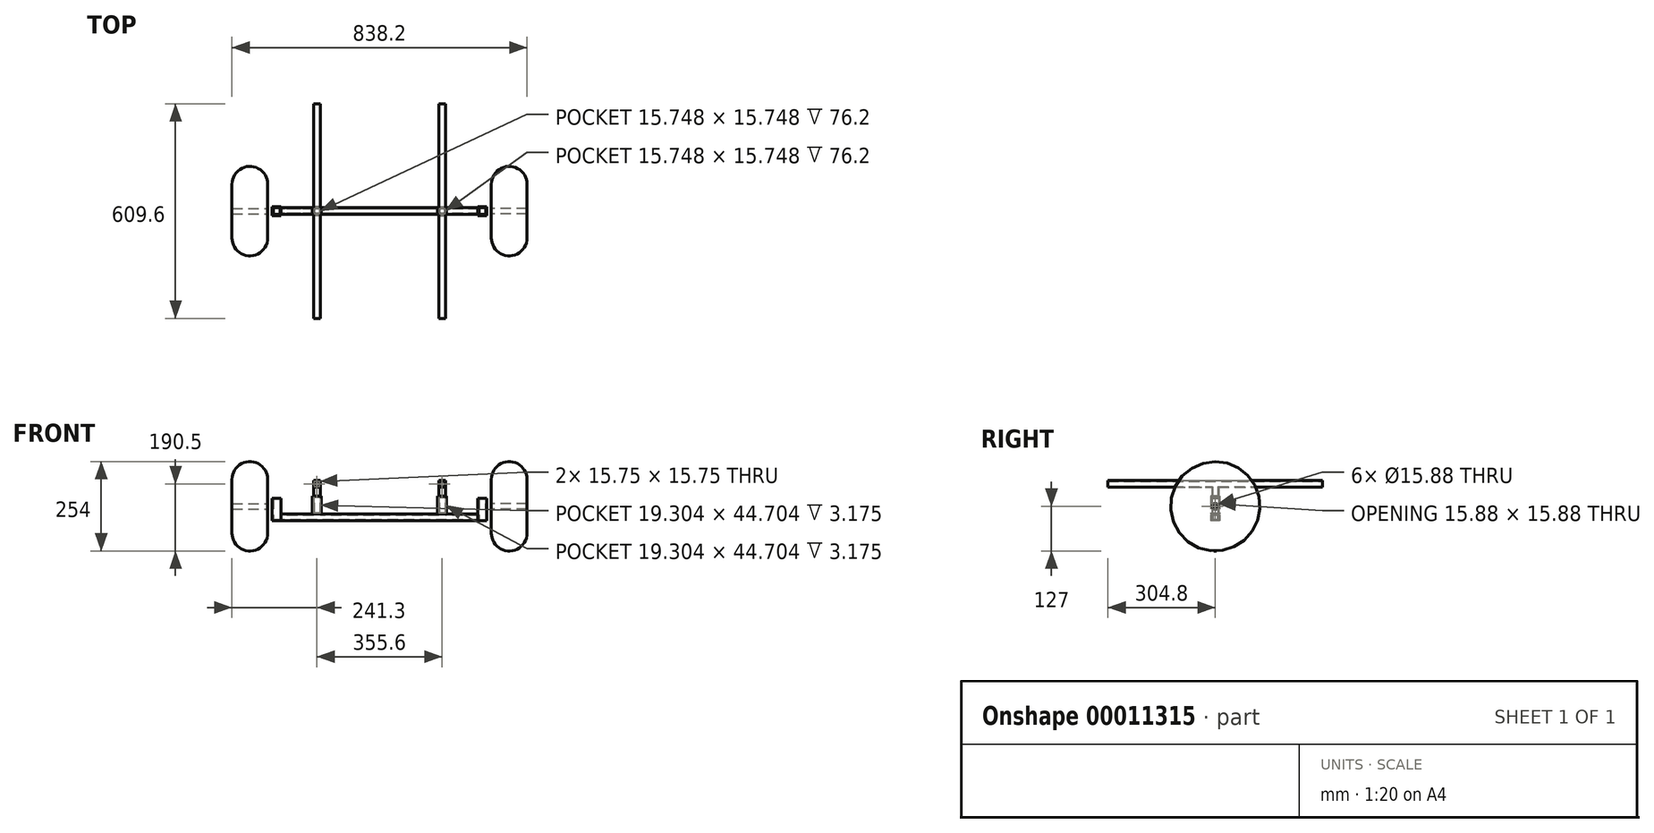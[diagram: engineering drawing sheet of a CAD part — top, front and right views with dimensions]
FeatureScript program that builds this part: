
annotation { "Feature Type Name" : "Feature", "Feature Type Description" : "" }
export const myFeature = defineFeature(function(context is Context, id is Id, definition is map)
    precondition{}
    {
        {
            var Q0;
            Q0=qCreatedBy(makeId("Front.planeOp"),FACE);
            var sketch = newSketch(context, id + "F0", { "sketchPlane" : qUnion([Q0])});
            skLineSegment(sketch, "E0.rect.bottom", {"start": v(279.4, 9.53) * mm, "end": v(-279.4, 9.53) * mm});
            skLineSegment(sketch, "E0.rect.top", {"start": v(279.4, -9.52) * mm, "end": v(-279.4, -9.52) * mm});
            skLineSegment(sketch, "E0.rect.left", {"start": v(279.4, 9.53) * mm, "end": v(279.4, -9.52) * mm});
            skLineSegment(sketch, "E0.rect.right", {"start": v(-279.4, 9.53) * mm, "end": v(-279.4, -9.52) * mm});
            skPoint(sketch, "E0.rect.middle", {"position": v(0, 0) * mm});
            skSolve(sketch);
        }
        {
            var Q0;
            Q0=makeQuery(id+"F0.imprint","IMPRINT",FACE,{"disambiguationData":[TD([[makeQuery(id+"F0.imprint","IMPRINT",EDGE,{"derivedFrom":sQuery(id+"F0.wireOp",EDGE,"E0.rect.bottom")}),1.0]])]});
            extrude(context, id + "F1", {"entities" : qUnion([Q0]), "endBound" : BoundingType.SYMMETRIC, "depth" : 19.05 * mm});
        }
        {
            var Q0;
            Q0=makeQuery(id+"F1.opExtrude","SWEPT_FACE",FACE,{"disambiguationData":[OSD([sQuery(id+"F0.wireOp",EDGE,"E0.rect.top")])]});
            var sketch = newSketch(context, id + "F2", { "sketchPlane" : qUnion([Q0])});
            skLineSegment(sketch, "E1.rect.bottom", {"start": v(-279.4, -12.7) * mm, "end": v(-304.8, -12.7) * mm});
            skLineSegment(sketch, "E1.rect.top", {"start": v(-279.4, 12.7) * mm, "end": v(-304.8, 12.7) * mm});
            skLineSegment(sketch, "E1.rect.left", {"start": v(-279.4, -12.7) * mm, "end": v(-279.4, 12.7) * mm});
            skLineSegment(sketch, "E1.rect.right", {"start": v(-304.8, -12.7) * mm, "end": v(-304.8, 12.7) * mm});
            skPoint(sketch, "E1.rect.middle", {"position": v(-292.1, 0) * mm});
            skLineSegment(sketch, "E2.0", {"start": v(-279.4, 9.53) * mm, "end": v(-279.4, -9.52) * mm, "construction": true});
            skLineSegment(sketch, "E3.0.MirrorCS", {"start": v(279.4, -12.7) * mm, "end": v(304.8, -12.7) * mm});
            skLineSegment(sketch, "E4.0.MirrorCS", {"start": v(304.8, -12.7) * mm, "end": v(304.8, 12.7) * mm});
            skLineSegment(sketch, "E5.0.MirrorCS", {"start": v(279.4, 12.7) * mm, "end": v(304.8, 12.7) * mm});
            skLineSegment(sketch, "E6.0.MirrorCS", {"start": v(279.4, -12.7) * mm, "end": v(279.4, 12.7) * mm});
            skSolve(sketch);
        }
        {
            var Q0;
            Q0 = qSketchRegion(id + "F2", true);
            extrude(context, id + "F3", {"entities" : qUnion([Q0]), "operationType" : NewBodyOperationType.ADD, "oppositeDirection" : true, "depth" : 63.5 * mm});
        }
        {
            var Q0;
            Q0=makeQuery(id+"F1.opExtrude","SWEPT_FACE",FACE,{"disambiguationData":[OSD([sQuery(id+"F0.wireOp",EDGE,"E0.rect.bottom")])]});
            var sketch = newSketch(context, id + "F4", { "sketchPlane" : qUnion([Q0])});
            skLineSegment(sketch, "E7.rect.bottom", {"start": v(-165.1, 12.7) * mm, "end": v(-190.5, 12.7) * mm});
            skLineSegment(sketch, "E7.rect.top", {"start": v(-165.1, -12.7) * mm, "end": v(-190.5, -12.7) * mm});
            skLineSegment(sketch, "E7.rect.left", {"start": v(-165.1, 12.7) * mm, "end": v(-165.1, -12.7) * mm});
            skLineSegment(sketch, "E7.rect.right", {"start": v(-190.5, 12.7) * mm, "end": v(-190.5, -12.7) * mm});
            skPoint(sketch, "E7.rect.middle", {"position": v(-177.8, 0) * mm});
            skLineSegment(sketch, "E8.0.MirrorCS", {"start": v(165.1, 12.7) * mm, "end": v(190.5, 12.7) * mm});
            skLineSegment(sketch, "E9.0.MirrorCS", {"start": v(190.5, 12.7) * mm, "end": v(190.5, -12.7) * mm});
            skLineSegment(sketch, "E10.0.MirrorCS", {"start": v(165.1, -12.7) * mm, "end": v(190.5, -12.7) * mm});
            skLineSegment(sketch, "E11.0.MirrorCS", {"start": v(165.1, 12.7) * mm, "end": v(165.1, -12.7) * mm});
            skSolve(sketch);
        }
        {
            var Q0;
            Q0 = qSketchRegion(id + "F4", true);
            extrude(context, id + "F5", {"entities" : qUnion([Q0]), "operationType" : NewBodyOperationType.ADD, "depth" : 50.8 * mm});
        }
        {
            var Q0;
            Q0=makeQuery(id+"F5.opExtrude","CAP_FACE",FACE,{"disambiguationData":[OSD([sQuery(id+"F4.wireOp",EDGE,"E7.rect.bottom"),sQuery(id+"F4.wireOp",EDGE,"E7.rect.top"),sQuery(id+"F4.wireOp",EDGE,"E7.rect.left"),sQuery(id+"F4.wireOp",EDGE,"E7.rect.right")])],"isStart":false});
            var sketch = newSketch(context, id + "F6", { "sketchPlane" : qUnion([Q0])});
            skLineSegment(sketch, "E12.0.0", {"start": v(-190.5, -12.7) * mm, "end": v(-165.1, -12.7) * mm, "construction": true});
            skLineSegment(sketch, "E12.0.1", {"start": v(-165.1, -12.7) * mm, "end": v(-165.1, 12.7) * mm, "construction": true});
            skLineSegment(sketch, "E12.0.2", {"start": v(-165.1, 12.7) * mm, "end": v(-190.5, 12.7) * mm, "construction": true});
            skLineSegment(sketch, "E12.0.3", {"start": v(-190.5, 12.7) * mm, "end": v(-190.5, -12.7) * mm, "construction": true});
            skLineSegment(sketch, "E13", {"start": v(-177.8, 12.7) * mm, "end": v(-177.8, -12.7) * mm, "construction": true});
            skLineSegment(sketch, "E14.rect.bottom", {"start": v(-168.28, -9.53) * mm, "end": v(-187.33, -9.53) * mm});
            skLineSegment(sketch, "E14.rect.top", {"start": v(-168.28, 9.52) * mm, "end": v(-187.33, 9.52) * mm});
            skLineSegment(sketch, "E14.rect.left", {"start": v(-168.28, -9.53) * mm, "end": v(-168.28, 9.52) * mm});
            skLineSegment(sketch, "E14.rect.right", {"start": v(-187.33, -9.53) * mm, "end": v(-187.33, 9.52) * mm});
            skPoint(sketch, "E14.rect.middle", {"position": v(-177.8, 0) * mm});
            skLineSegment(sketch, "E15.0.MirrorCS", {"start": v(168.28, 9.52) * mm, "end": v(187.33, 9.52) * mm});
            skLineSegment(sketch, "E16.0.MirrorCS", {"start": v(187.33, -9.53) * mm, "end": v(187.33, 9.52) * mm});
            skLineSegment(sketch, "E17.0.MirrorCS", {"start": v(168.28, -9.53) * mm, "end": v(187.33, -9.53) * mm});
            skLineSegment(sketch, "E18.0.MirrorCS", {"start": v(168.28, -9.53) * mm, "end": v(168.28, 9.52) * mm});
            skSolve(sketch);
        }
        {
            var Q0;
            Q0=makeQuery(id+"F6.imprint","IMPRINT",FACE,{"disambiguationData":[TD([[makeQuery(id+"F6.imprint","IMPRINT",EDGE,{"derivedFrom":sQuery(id+"F6.wireOp",EDGE,"E14.rect.bottom")}),-1.0]])]});
            var Q1;
            Q1=makeQuery(id+"F6.imprint","IMPRINT",FACE,{"disambiguationData":[TD([[makeQuery(id+"F6.imprint","IMPRINT",EDGE,{"derivedFrom":sQuery(id+"F6.wireOp",EDGE,"E15.0.MirrorCS")}),-1.0]])]});
            var Q2;
            {var subQ0=sQuery(id+"F0.wireOp",EDGE,"E0.rect.bottom");Q2=makeQuery(id+"F5.boolean.opBoolean","SPLIT",FACE,{"disambiguationData":[TD([makeQuery(id+"F3.opExtrude","SWEPT_FACE",FACE,{"disambiguationData":[OSD([sQuery(id+"F2.wireOp",EDGE,"E1.rect.left")])]})])],"derivedFrom":makeQuery(id+"F1.opExtrude","SWEPT_FACE",FACE,{"disambiguationData":[OSD([subQ0])]})});}
            extrude(context, id + "F7", {"entities" : qUnion([Q0, Q1]), "depth" : 25.4 * mm, "hasSecondDirection" : true, "secondDirectionBound" : SecondDirectionBoundingType.UP_TO_SURFACE, "secondDirectionOppositeDirection" : true, "secondDirectionBoundEntityFace" : qUnion([Q2]), "secondDirectionDepth" : 25.4 * mm});
        }
        {
            var Q0;
            Q0=qCreatedBy(makeId("Front.planeOp"),FACE);
            var sketch = newSketch(context, id + "F8", { "sketchPlane" : qUnion([Q0])});
            skPoint(sketch, "E19.0", {"position": v(-187.33, 85.72) * mm});
            skPoint(sketch, "E20.0", {"position": v(-168.28, 85.72) * mm});
            skLineSegment(sketch, "E21.bottom", {"start": v(-168.28, 85.72) * mm, "end": v(-187.33, 85.72) * mm});
            skLineSegment(sketch, "E21.top", {"start": v(-168.28, 104.77) * mm, "end": v(-187.33, 104.77) * mm});
            skLineSegment(sketch, "E21.left", {"start": v(-168.28, 85.72) * mm, "end": v(-168.28, 104.77) * mm});
            skLineSegment(sketch, "E21.right", {"start": v(-187.33, 85.72) * mm, "end": v(-187.33, 104.77) * mm});
            skLineSegment(sketch, "E22.0.MirrorCS", {"start": v(168.28, 104.77) * mm, "end": v(187.33, 104.77) * mm});
            skLineSegment(sketch, "E23.0.MirrorCS", {"start": v(187.33, 85.72) * mm, "end": v(187.33, 104.77) * mm});
            skLineSegment(sketch, "E24.0.MirrorCS", {"start": v(168.28, 85.72) * mm, "end": v(168.28, 104.77) * mm});
            skLineSegment(sketch, "E25.0.MirrorCS", {"start": v(168.28, 85.72) * mm, "end": v(187.33, 85.72) * mm});
            skSolve(sketch);
        }
        {
            var Q0;
            Q0=makeQuery(id+"F8.imprint","IMPRINT",FACE,{"disambiguationData":[TD([[makeQuery(id+"F8.imprint","IMPRINT",EDGE,{"derivedFrom":sQuery(id+"F8.wireOp",EDGE,"E21.bottom")}),-1.0]])]});
            var Q1;
            Q1=makeQuery(id+"F8.imprint","IMPRINT",FACE,{"disambiguationData":[TD([[makeQuery(id+"F8.imprint","IMPRINT",EDGE,{"derivedFrom":sQuery(id+"F8.wireOp",EDGE,"E22.0.MirrorCS")}),-1.0]])]});
            extrude(context, id + "F9", {"entities" : qUnion([Q0, Q1]), "operationType" : NewBodyOperationType.ADD, "endBound" : BoundingType.SYMMETRIC, "depth" : 609.6 * mm});
        }
        {
            var Q0;
            Q0=makeQuery(id+"F9.opExtrude","CAP_FACE",FACE,{"disambiguationData":[OSD([sQuery(id+"F8.wireOp",EDGE,"E21.bottom"),sQuery(id+"F8.wireOp",EDGE,"E21.top"),sQuery(id+"F8.wireOp",EDGE,"E21.left"),sQuery(id+"F8.wireOp",EDGE,"E21.right")])],"isStart":false});
            var Q1;
            Q1=makeQuery(id+"F9.opExtrude","CAP_FACE",FACE,{"disambiguationData":[OSD([sQuery(id+"F8.wireOp",EDGE,"E21.bottom"),sQuery(id+"F8.wireOp",EDGE,"E21.top"),sQuery(id+"F8.wireOp",EDGE,"E21.left"),sQuery(id+"F8.wireOp",EDGE,"E21.right")])],"isStart":true});
            var Q2;
            Q2=makeQuery(id+"F9.opExtrude","CAP_FACE",FACE,{"disambiguationData":[OSD([sQuery(id+"F8.wireOp",EDGE,"E22.0.MirrorCS"),sQuery(id+"F8.wireOp",EDGE,"E23.0.MirrorCS"),sQuery(id+"F8.wireOp",EDGE,"E24.0.MirrorCS"),sQuery(id+"F8.wireOp",EDGE,"E25.0.MirrorCS")])],"isStart":true});
            var Q3;
            Q3=makeQuery(id+"F9.opExtrude","CAP_FACE",FACE,{"disambiguationData":[OSD([sQuery(id+"F8.wireOp",EDGE,"E22.0.MirrorCS"),sQuery(id+"F8.wireOp",EDGE,"E23.0.MirrorCS"),sQuery(id+"F8.wireOp",EDGE,"E24.0.MirrorCS"),sQuery(id+"F8.wireOp",EDGE,"E25.0.MirrorCS")])],"isStart":false});
            shell(context, id + "F10", {"entities" : qUnion([Q0, Q1, Q2, Q3]), "thickness" : 1.65 * mm});
        }
        {
            var Q0;
            Q0=makeQuery(id+"F3.opExtrude","CAP_FACE",FACE,{"disambiguationData":[OSD([sQuery(id+"F2.wireOp",EDGE,"E1.rect.bottom"),sQuery(id+"F2.wireOp",EDGE,"E1.rect.top"),sQuery(id+"F2.wireOp",EDGE,"E1.rect.left"),sQuery(id+"F2.wireOp",EDGE,"E1.rect.right")])],"isStart":false});
            var Q1;
            Q1=makeQuery(id+"F3.opExtrude","CAP_FACE",FACE,{"disambiguationData":[OSD([sQuery(id+"F2.wireOp",EDGE,"E3.0.MirrorCS"),sQuery(id+"F2.wireOp",EDGE,"E4.0.MirrorCS"),sQuery(id+"F2.wireOp",EDGE,"E5.0.MirrorCS"),sQuery(id+"F2.wireOp",EDGE,"E6.0.MirrorCS")])],"isStart":false});
            shell(context, id + "F11", {"entities" : qUnion([Q0, Q1]), "thickness" : 3.05 * mm});
        }
        {
            var Q0;
            Q0=makeQuery(id+"F3.opExtrude","SWEPT_FACE",FACE,{"disambiguationData":[OSD([sQuery(id+"F2.wireOp",EDGE,"E1.rect.right")])]});
            cPlane(context, id + "F12", {"entities" : qUnion([Q0]), "cplaneType" : CPlaneType.OFFSET, "offset" : 63.5 * mm, "width" : 152.4 * mm, "height" : 152.4 * mm});
        }
        {
            var Q0;
            Q0=qCreatedBy(id+"F12.planeOp",FACE);
            var sketch = newSketch(context, id + "F13", { "sketchPlane" : qUnion([Q0])});
            skPoint(sketch, "E26.0", {"position": v(0, 0) * mm});
            skCircle(sketch, "E27", {"center": v(0, 31.75) * mm, "radius": 7.94 * mm});
            skCircle(sketch, "E28", {"center": v(0, 31.75) * mm, "radius": 127 * mm});
            skSolve(sketch);
        }
        {
            var Q0;
            Q0=makeQuery(id+"F13.imprint","IMPRINT",FACE,{"disambiguationData":[TD([[makeQuery(id+"F13.imprint","IMPRINT",EDGE,{"derivedFrom":sQuery(id+"F13.wireOp",EDGE,"c96f1c67-846e-4751-9587-819ac5c1c182.0")}),-1.0]])]});
            var Q1;
            Q1=makeQuery(id+"F13.imprint","IMPRINT",FACE,{"disambiguationData":[TD([[makeQuery(id+"F13.imprint","IMPRINT",EDGE,{"derivedFrom":sQuery(id+"F13.wireOp",EDGE,"E27")}),-1.0]])]});
            extrude(context, id + "F14", {"entities" : qUnion([Q0, Q1]), "endBound" : BoundingType.SYMMETRIC, "depth" : 101.6 * mm});
        }
        {
            var Q0;
            Q0=makeQuery(id+"F14.opExtrude","CAP_EDGE",EDGE,{"disambiguationData":[OSD([sQuery(id+"F13.wireOp",EDGE,"E28")])],"isStart":true});
            var Q1;
            Q1=makeQuery(id+"F14.opExtrude","CAP_EDGE",EDGE,{"disambiguationData":[OSD([sQuery(id+"F13.wireOp",EDGE,"E28")])],"isStart":false});
            fillet(context, id + "F15", {"entities" : qUnion([Q0, Q1]), "radius" : 50.8 * mm, "tangentPropagation" : true, "allowEdgeOverflow" : false});
        }
        {
            var Q0;
            Q0=makeQuery(id+"F3.opExtrude","SWEPT_FACE",FACE,{"disambiguationData":[OSD([sQuery(id+"F2.wireOp",EDGE,"E1.rect.right")])]});
            var sketch = newSketch(context, id + "F16", { "sketchPlane" : qUnion([Q0])});
            skCircle(sketch, "E29.0", {"center": v(0, 31.75) * mm, "radius": 7.94 * mm});
            skSolve(sketch);
        }
        {
            var Q0;
            Q0=makeQuery(id+"F16.imprint","IMPRINT",FACE,{"disambiguationData":[TD([[makeQuery(id+"F16.imprint","IMPRINT",EDGE,{"derivedFrom":sQuery(id+"F16.wireOp",EDGE,"E29.0")}),1.0]])]});
            var Q1;
            Q1=makeQuery(id+"F3.opExtrude","SWEPT_FACE",FACE,{"disambiguationData":[OSD([sQuery(id+"F2.wireOp",EDGE,"E1.rect.left")])]});
            extrude(context, id + "F17", {"entities" : qUnion([Q0]), "operationType" : NewBodyOperationType.REMOVE, "endBound" : BoundingType.UP_TO_SURFACE, "oppositeDirection" : true, "endBoundEntityFace" : qUnion([Q1]), "depth" : 25.4 * mm});
        }
        {
            var Q0;
            Q0=makeQuery(id+"F14.opExtrude","SWEPT_BODY",BODY,{"disambiguationData":[OSD([sQuery(id+"F13.wireOp",EDGE,"E27"),sQuery(id+"F13.wireOp",EDGE,"E28")])]});
            var Q1;
            Q1=qCreatedBy(makeId("Right.planeOp"),FACE);
            mirror(context, id + "F18", {"entities" : qUnion([Q0]), "mirrorPlane" : qUnion([Q1])});
        }
        {
            var Q0;
            {var subQ0=sQuery(id+"F2.wireOp",EDGE,"E1.rect.left");var subQ1=makeQuery(id+"F17.opExtrude","SWEPT_FACE",FACE,{"disambiguationData":[OSD([sQuery(id+"F16.wireOp",EDGE,"E29.0")])]});var subQ2=sQuery(id+"F2.wireOp",EDGE,"E1.rect.right");Q0=qUnion([makeQuery(id+"F17.boolean.opBoolean","COPY",FACE,{"disambiguationData":[TD([makeQuery(id+"F3.opExtrude","SWEPT_FACE",FACE,{"disambiguationData":[OSD([subQ2])]})])],"derivedFrom":subQ1}),makeQuery(id+"F17.boolean.opBoolean","COPY",FACE,{"disambiguationData":[TD([makeQuery(id+"F3.opExtrude","SWEPT_FACE",FACE,{"disambiguationData":[OSD([subQ0])]})])],"derivedFrom":subQ1})]);}
            var Q1;
            Q1=qCreatedBy(makeId("Right.planeOp"),FACE);
            mirror(context, id + "F19", {"faces" : qUnion([Q0]), "mirrorPlane" : qUnion([Q1]), "patternType" : MirrorType.FACE});
        }
    });
